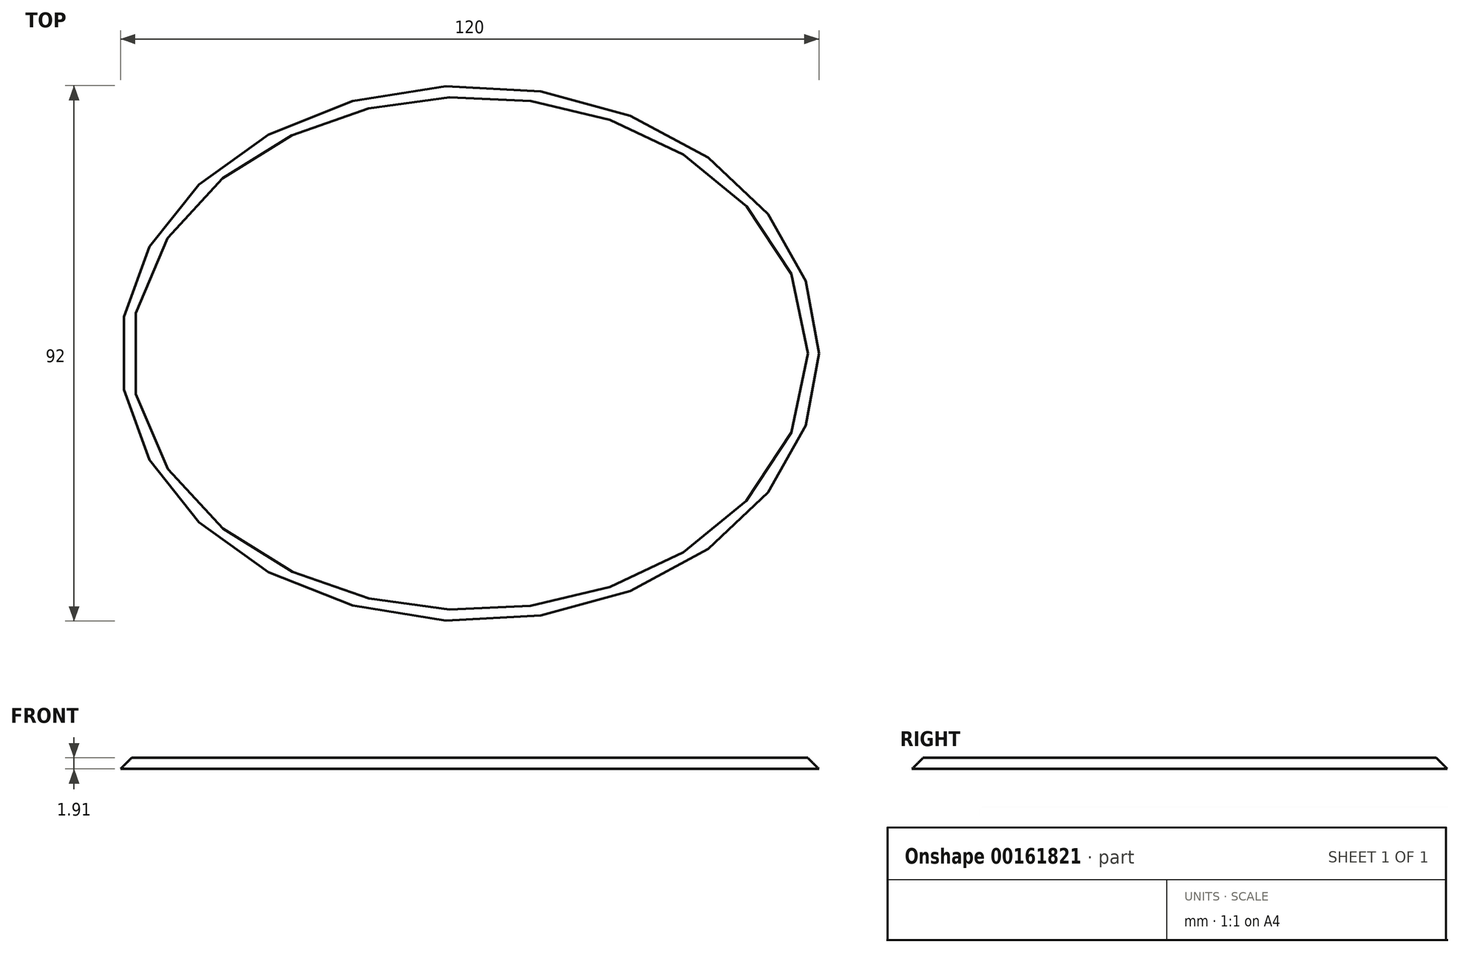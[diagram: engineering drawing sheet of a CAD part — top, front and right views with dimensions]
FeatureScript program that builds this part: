
annotation { "Feature Type Name" : "Feature", "Feature Type Description" : "" }
export const myFeature = defineFeature(function(context is Context, id is Id, definition is map)
    precondition{}
    {
        {
            var Q0;
            Q0=qCreatedBy(makeId("Top.planeOp"),FACE);
            var sketch = newSketch(context, id + "F0", { "sketchPlane" : qUnion([Q0])});
            skEllipse(sketch, "E0", {"center": v(0, 0) * mm, "majorRadius": 60 * mm, "minorRadius": 46 * mm, "majorAxis": v(1, 0)});
            skSolve(sketch);
        }
        {
            var Q0;
            Q0 = qSketchRegion(id + "F0", true);
            extrude(context, id + "F1", {"entities" : qUnion([Q0]), "depth" : 1.9 * mm, "offsetDistance" : 25.4 * mm});
        }
        {
            var Q0;
            Q0=makeQuery(id+"F1.opExtrude","CAP_EDGE",EDGE,{"disambiguationData":[OSD([sQuery(id+"F0.wireOp",EDGE,"E0")])],"isStart":false});
            chamfer(context, id + "F2", {"entities" : qUnion([Q0]), "width" : 1.9 * mm, "tangentPropagation" : true});
        }
    });
